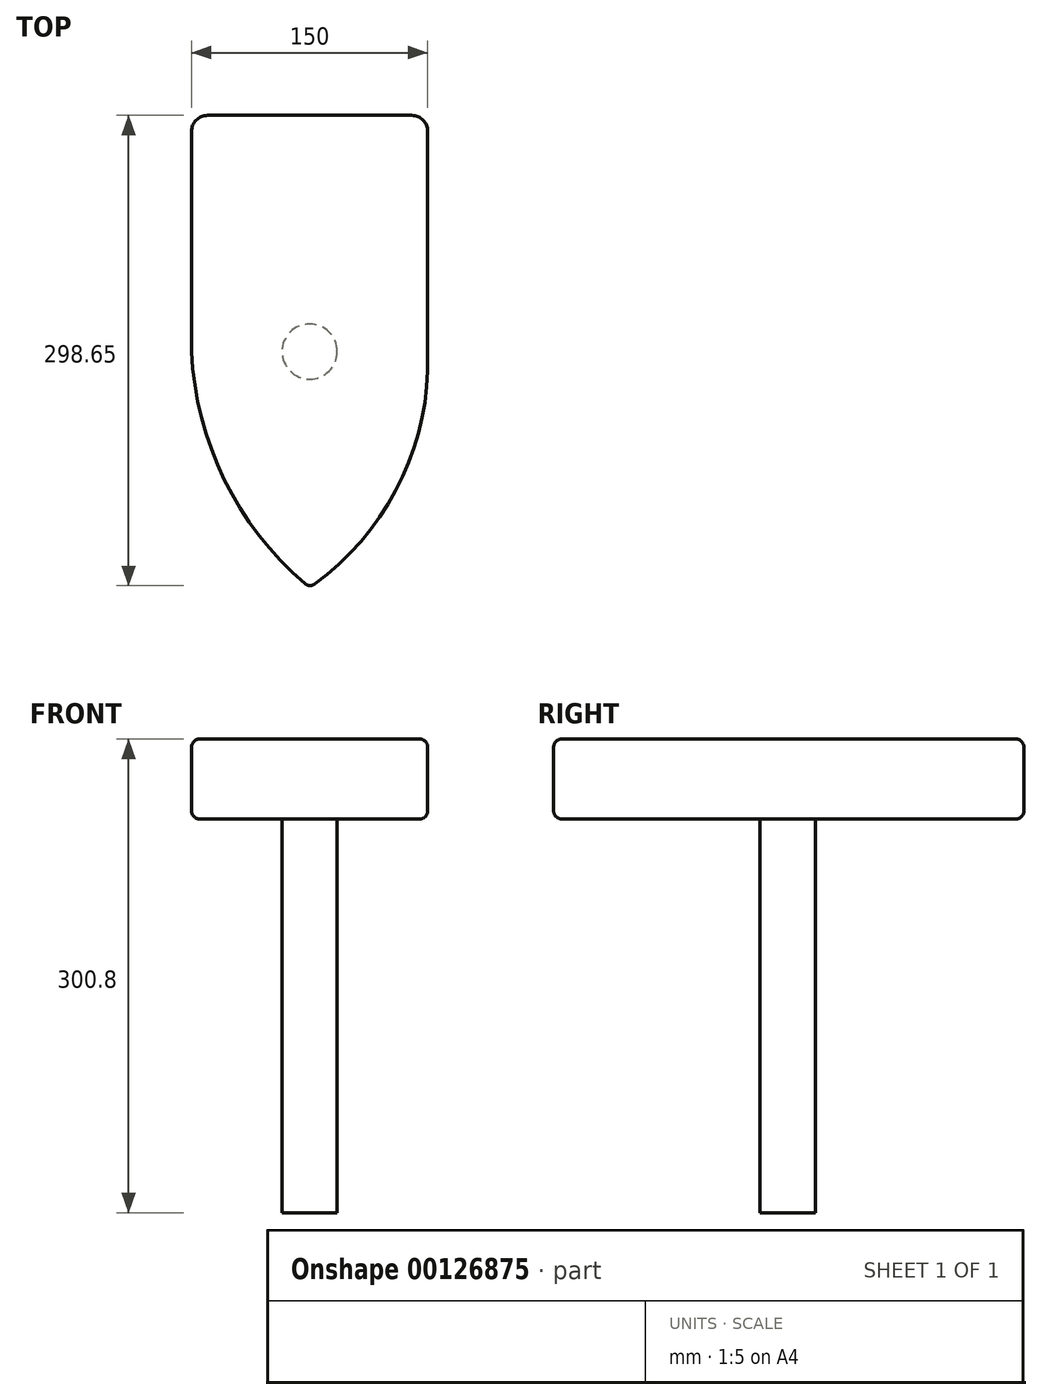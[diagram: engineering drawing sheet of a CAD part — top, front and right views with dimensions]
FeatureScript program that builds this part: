
annotation { "Feature Type Name" : "Feature", "Feature Type Description" : "" }
export const myFeature = defineFeature(function(context is Context, id is Id, definition is map)
    precondition{}
    {
        {
            var Q0;
            Q0=qCreatedBy(makeId("Top.planeOp"),FACE);
            var sketch = newSketch(context, id + "F0", { "sketchPlane" : qUnion([Q0])});
            skCircle(sketch, "E0", {"center": v(-6.46, 6.95) * mm, "radius": 17.5 * mm});
            skSolve(sketch);
        }
        {
            var Q0;
            Q0=makeQuery(id+"F0.imprint","IMPRINT",FACE,{"disambiguationData":[TD([[makeQuery(id+"F0.imprint","IMPRINT",EDGE,{"derivedFrom":sQuery(id+"F0.wireOp",EDGE,"E0")}),1.0]])]});
            extrude(context, id + "F1", {"entities" : qUnion([Q0]), "depth" : 250 * mm});
        }
        {
            var Q0;
            Q0=makeQuery(id+"F1.opExtrude","CAP_FACE",FACE,{"disambiguationData":[OSD([sQuery(id+"F0.wireOp",EDGE,"E0")])],"isStart":false});
            var sketch = newSketch(context, id + "F2", { "sketchPlane" : qUnion([Q0])});
            skPoint(sketch, "E1", {"position": v(-6.46, 6.95) * mm});
            skLineSegment(sketch, "E2.bottom", {"start": v(68.54, 156.95) * mm, "end": v(-81.46, 156.95) * mm});
            skLineSegment(sketch, "E2.top", {"start": v(68.54, -143.05) * mm, "end": v(-81.46, -143.05) * mm});
            skLineSegment(sketch, "E2.left", {"start": v(68.54, 156.95) * mm, "end": v(68.54, -143.05) * mm});
            skLineSegment(sketch, "E2.right", {"start": v(-81.46, 156.95) * mm, "end": v(-81.46, -143.05) * mm});
            skSolve(sketch);
        }
        {
            var Q0;
            Q0=makeQuery(id+"F2.imprint","IMPRINT",FACE,{"disambiguationData":[TD([[makeQuery(id+"F2.imprint","IMPRINT",EDGE,{"derivedFrom":makeQuery(id+"F1.opExtrude","CAP_EDGE",EDGE,{"disambiguationData":[OSD([sQuery(id+"F0.wireOp",EDGE,"E0")])],"isStart":false})}),1.0]])]});
            var Q1;
            Q1=makeQuery(id+"F2.imprint","IMPRINT",FACE,{"disambiguationData":[TD([[makeQuery(id+"F2.imprint","IMPRINT",EDGE,{"derivedFrom":sQuery(id+"F2.wireOp",EDGE,"E2.bottom")}),1.0]])]});
            extrude(context, id + "F3", {"entities" : qUnion([Q0, Q1]), "operationType" : NewBodyOperationType.ADD, "depth" : 50.8 * mm});
        }
        {
            var Q0;
            Q0=makeQuery(id+"F3.opExtrude","CAP_FACE",FACE,{"disambiguationData":[OSD([sQuery(id+"F2.wireOp",EDGE,"E2.bottom"),sQuery(id+"F2.wireOp",EDGE,"E2.top"),sQuery(id+"F2.wireOp",EDGE,"E2.left"),sQuery(id+"F2.wireOp",EDGE,"E2.right")])],"isStart":false});
            var sketch = newSketch(context, id + "F4", { "sketchPlane" : qUnion([Q0])});
            skPoint(sketch, "E3", {"position": v(-6.46, -143.05) * mm});
            skPoint(sketch, "E4", {"position": v(68.54, 6.95) * mm});
            skArc(sketch, "E5", {"start": v(-6.46, -143.05) * mm, "mid": v(50.13, -77.6) * mm, "end": v(68.54, 6.95) * mm});
            skLineSegment(sketch, "E6", {"start": v(-6.46, -143.05) * mm, "end": v(68.54, -143.05) * mm});
            skLineSegment(sketch, "E7", {"start": v(68.54, -143.05) * mm, "end": v(68.54, 6.95) * mm});
            skSolve(sketch);
        }
        {
            var Q0;
            {var subQ0=sQuery(id+"F4.wireOp",EDGE,"E7");var subQ1=sQuery(id+"F4.wireOp",EDGE,"E5");var subQ3=makeQuery(id+"F4.imprint","INTERSECT",VERTEX,{"derivedFrom":[subQ1,subQ0]});Q0=makeQuery(id+"F4.imprint","IMPRINT",FACE,{"disambiguationData":[TD([[makeQuery(id+"F4.imprint","IMPRINT",EDGE,{"disambiguationData":[TD([[subQ3,-1.0]])],"derivedFrom":subQ1}),1.0]])]});}
            var Q1;
            {var subQ0=sQuery(id+"F4.wireOp",EDGE,"E6");Q1=makeQuery(id+"F4.imprint","IMPRINT",FACE,{"disambiguationData":[TD([[makeQuery(id+"F4.imprint","IMPRINT",EDGE,{"derivedFrom":subQ0}),-1.0]])]});}
            extrude(context, id + "F5", {"entities" : qUnion([Q0, Q1]), "operationType" : NewBodyOperationType.REMOVE, "oppositeDirection" : true, "depth" : 50.8 * mm});
        }
        {
            var Q0;
            Q0=makeQuery(id+"F3.opExtrude","CAP_FACE",FACE,{"disambiguationData":[OSD([sQuery(id+"F2.wireOp",EDGE,"E2.bottom"),sQuery(id+"F2.wireOp",EDGE,"E2.top"),sQuery(id+"F2.wireOp",EDGE,"E2.left"),sQuery(id+"F2.wireOp",EDGE,"E2.right")])],"isStart":false});
            var sketch = newSketch(context, id + "F6", { "sketchPlane" : qUnion([Q0])});
            skArc(sketch, "E8", {"start": v(-81.46, 6.95) * mm, "mid": v(-59.8, -75.96) * mm, "end": v(-6.46, -143.05) * mm});
            skLineSegment(sketch, "E9", {"start": v(-81.46, 6.95) * mm, "end": v(-81.46, -143.05) * mm});
            skLineSegment(sketch, "E10", {"start": v(-81.46, -143.05) * mm, "end": v(-6.46, -143.05) * mm});
            skSolve(sketch);
        }
        {
            var Q0;
            Q0 = qSketchRegion(id + "F6", true);
            extrude(context, id + "F7", {"entities" : qUnion([Q0]), "operationType" : NewBodyOperationType.REMOVE, "oppositeDirection" : true, "depth" : 50.8 * mm});
        }
        {
            var Q0;
            Q0=makeQuery(id+"F3.opExtrude","SWEPT_EDGE",EDGE,{"disambiguationData":[OSD([sQuery(id+"F2.wireOp",EDGE,"E2.bottom"),sQuery(id+"F2.wireOp",EDGE,"E2.right")])]});
            var Q1;
            Q1=makeQuery(id+"F3.opExtrude","SWEPT_EDGE",EDGE,{"disambiguationData":[OSD([sQuery(id+"F2.wireOp",EDGE,"E2.bottom"),sQuery(id+"F2.wireOp",EDGE,"E2.left")])]});
            fillet(context, id + "F8", {"entities" : qUnion([Q0, Q1]), "radius" : 10.16 * mm, "tangentPropagation" : true, "allowEdgeOverflow" : false});
        }
        {
            var Q0;
            Q0=makeQuery(id+"F3.opExtrude","SWEPT_FACE",FACE,{"disambiguationData":[OSD([sQuery(id+"F2.wireOp",EDGE,"E2.bottom")])]});
            var Q1;
            Q1=makeQuery(id+"F3.opExtrude","SWEPT_FACE",FACE,{"disambiguationData":[OSD([sQuery(id+"F2.wireOp",EDGE,"E2.right")])]});
            var Q2;
            Q2=makeQuery(id+"F7.boolean.opBoolean","COPY",FACE,{"derivedFrom":makeQuery(id+"F7.opExtrude","SWEPT_FACE",FACE,{"disambiguationData":[OSD([sQuery(id+"F6.wireOp",EDGE,"E8")])]})});
            var Q3;
            Q3=makeQuery(id+"F3.opExtrude","SWEPT_FACE",FACE,{"disambiguationData":[OSD([sQuery(id+"F2.wireOp",EDGE,"E2.left")])]});
            var Q4;
            {var subQ0=sQuery(id+"F4.wireOp",EDGE,"E5");Q4=makeQuery(id+"F5.boolean.opBoolean","COPY",FACE,{"derivedFrom":makeQuery(id+"F5.opExtrude","SWEPT_FACE",FACE,{"disambiguationData":[OSD([subQ0]),TDD([makeQuery(id+"F4.imprint","IMPRINT",EDGE,{"disambiguationData":[TD([[makeQuery(id+"F4.imprint","INTERSECT",VERTEX,{"derivedFrom":[subQ0,sQuery(id+"F4.wireOp",EDGE,"E7")]}),1.0]])],"derivedFrom":subQ0})])]})});}
            var Q5;
            {var subQ0=sQuery(id+"F4.wireOp",EDGE,"E5");Q5=makeQuery(id+"F7.boolean.opBoolean","MERGE",EDGE,{"derivedFrom":[makeQuery(id+"F5.boolean.opBoolean","COPY",EDGE,{"derivedFrom":makeQuery(id+"F5.opExtrude","SWEPT_EDGE",EDGE,{"disambiguationData":[OSD([sQuery(id+"F2.wireOp",EDGE,"E2.top"),subQ0,sQuery(id+"F4.wireOp",EDGE,"E6")])]})}),makeQuery(id+"F7.opExtrude","SWEPT_EDGE",EDGE,{"disambiguationData":[OSD([subQ0,sQuery(id+"F6.wireOp",EDGE,"E8"),sQuery(id+"F6.wireOp",EDGE,"E10")])]})]});}
            fillet(context, id + "F9", {"entities" : qUnion([Q0, Q1, Q2, Q3, Q4, Q5]), "radius" : 5.08 * mm, "tangentPropagation" : true, "allowEdgeOverflow" : false});
        }
    });
